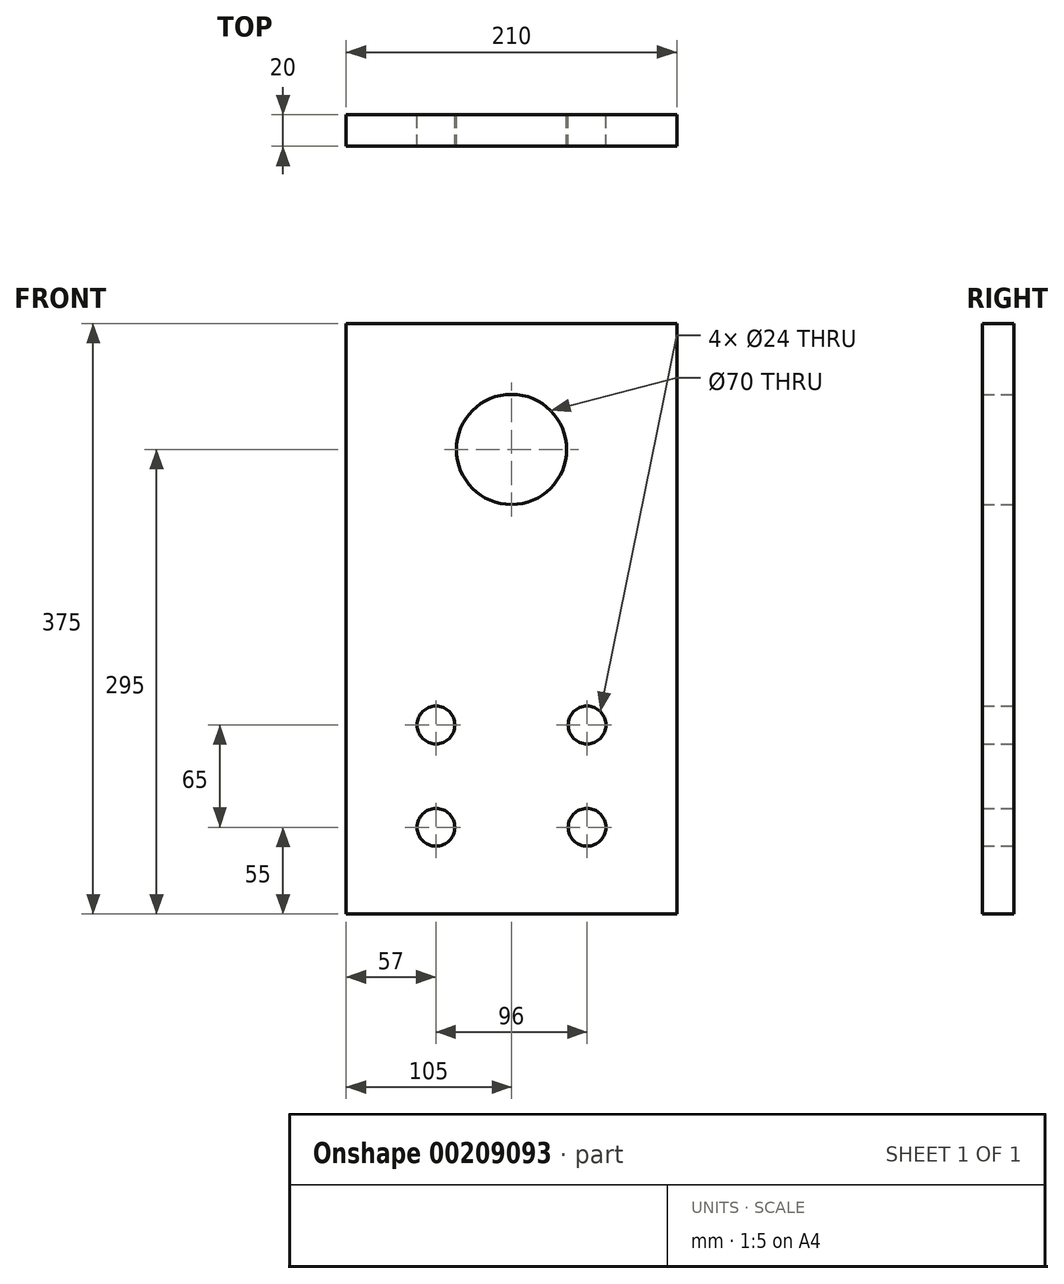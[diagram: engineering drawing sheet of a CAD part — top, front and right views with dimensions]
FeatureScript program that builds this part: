
annotation { "Feature Type Name" : "Feature", "Feature Type Description" : "" }
export const myFeature = defineFeature(function(context is Context, id is Id, definition is map)
    precondition{}
    {
        {
            var Q0;
            Q0=qCreatedBy(makeId("Front.planeOp"),FACE);
            var sketch = newSketch(context, id + "F0", { "sketchPlane" : qUnion([Q0])});
            skLineSegment(sketch, "E0.bottom", {"start": v(105, -187.5) * mm, "end": v(-105, -187.5) * mm});
            skLineSegment(sketch, "E0.top", {"start": v(105, 187.5) * mm, "end": v(-105, 187.5) * mm});
            skLineSegment(sketch, "E0.left", {"start": v(105, -187.5) * mm, "end": v(105, 187.5) * mm});
            skLineSegment(sketch, "E0.right", {"start": v(-105, -187.5) * mm, "end": v(-105, 187.5) * mm});
            skPoint(sketch, "E0.middle", {"position": v(0, 0) * mm});
            skCircle(sketch, "E1", {"center": v(-48, -132.5) * mm, "radius": 12 * mm});
            skCircle(sketch, "E2", {"center": v(-48, -67.5) * mm, "radius": 12 * mm});
            skCircle(sketch, "E3.MirrorC", {"center": v(48, -67.5) * mm, "radius": 12 * mm});
            skCircle(sketch, "E4.MirrorC", {"center": v(48, -132.5) * mm, "radius": 12 * mm});
            skCircle(sketch, "E5", {"center": v(0, 107.5) * mm, "radius": 35 * mm});
            skSolve(sketch);
        }
        {
            var Q0;
            Q0=qSketchRegion(id+"F0",true);
            extrude(context, id + "F1", {"entities" : qUnion([Q0]), "depth" : 20 * mm, "symmetric" : true});
        }
    });
